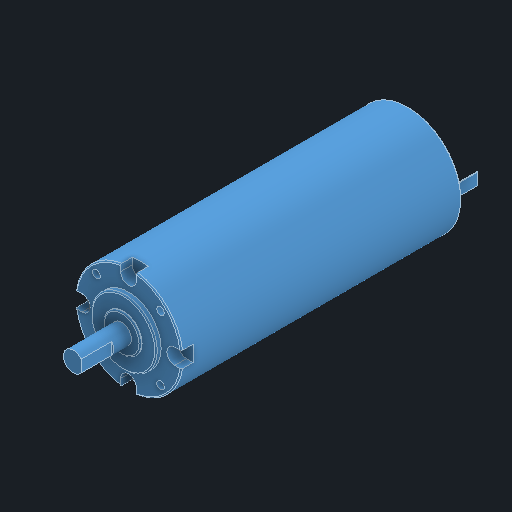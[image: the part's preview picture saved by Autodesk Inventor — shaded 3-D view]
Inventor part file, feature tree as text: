
AUTODESK INVENTOR PART (.ipt)
format: ipt  version: 2024 (Build 280153000, 153)  size: 339,456 bytes
history: native  units: mm
features: extrude x11, sketch x11, pattern_circular x2, other x1, fillet x1, chamfer x1
ambient origin geometry x8: Origin, YZ Plane, XZ Plane, XY Plane, X Axis, Y Axis, Z Axis, Center Point
bodies: Body1 (feature_tree)
feature tree (27):
  other  "Твердое тело1"
  extrude  "Выдавливание1"  Depth=42.0mm
  extrude  "Выдавливание2"  Depth=110.0mm TaperAngle=0.0deg
  extrude  "Выдавливание3"  Depth=25.7mm
  pattern_circular  "Круговой массив1"  [2 undecoded]
  extrude  "Выдавливание4"  Depth=6.2mm
  pattern_circular  "Круговой массив2"  [2 undecoded]
  extrude  "Выдавливание5"  Depth=4.6mm TaperAngle=0.0deg
  extrude  "Выдавливание6"  Depth=40.0mm TaperAngle=360.0deg
  extrude  "Выдавливание7"  Depth=3.0mm
  extrude  "Выдавливание8"  Depth=3.2mm
  extrude  "Выдавливание9"  Depth=7.0mm TaperAngle=0.0deg
  extrude  "Выдавливание10"  Depth=40.0mm TaperAngle=360.0deg
  extrude  "Выдавливание11"  Depth=14.7mm
  fillet  "Сопряжение1"  Radius=0.7mm
  chamfer  "Фаска1"  Distance=7.8mm
  sketch  "Эскиз1"
  sketch  "Эскиз2"
  sketch  "Эскиз3"
  sketch  "Эскиз4"
  sketch  "Эскиз5"
  sketch  "Эскиз6"
  sketch  "Эскиз7"
  sketch  "Эскиз8"
  sketch  "Эскиз9"
  sketch  "Эскиз10"
  sketch  "Эскиз11"
note: 4 required parameter values undecoded (feature->parameter linkage not recoverable at this tier; creation-order binding heuristic only, values carry confidence <= 0.55)
